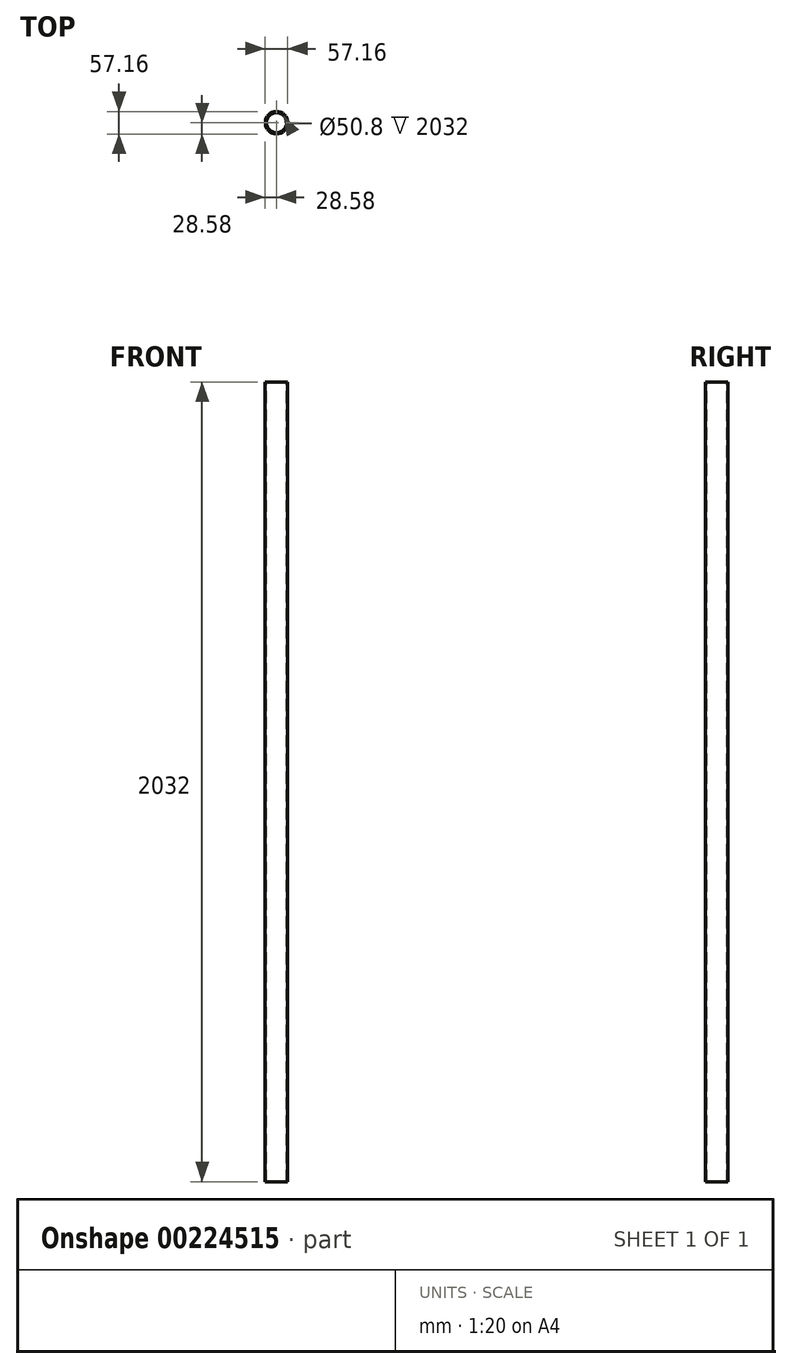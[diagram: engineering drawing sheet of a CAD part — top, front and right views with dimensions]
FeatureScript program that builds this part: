
annotation { "Feature Type Name" : "Feature", "Feature Type Description" : "" }
export const myFeature = defineFeature(function(context is Context, id is Id, definition is map)
    precondition{}
    {
        {
            var Q0;
            Q0=qCreatedBy(makeId("Top.planeOp"),FACE);
            var sketch = newSketch(context, id + "F0", { "sketchPlane" : qUnion([Q0])});
            skCircle(sketch, "E0", {"center": v(0, 0) * mm, "radius": 25.4 * mm});
            skCircle(sketch, "E1.0", {"center": v(0, 0) * mm, "radius": 28.58 * mm});
            skSolve(sketch);
        }
        {
            var Q0;
            Q0=makeQuery(id+"F0.imprint","IMPRINT",FACE,{"disambiguationData":[TD([[makeQuery(id+"F0.imprint","IMPRINT",EDGE,{"derivedFrom":sQuery(id+"F0.wireOp",EDGE,"E0")}),-1.0]])]});
            extrude(context, id + "F1", {"entities" : qUnion([Q0]), "oppositeDirection" : true, "depth" : 2032 * mm});
        }
    });
